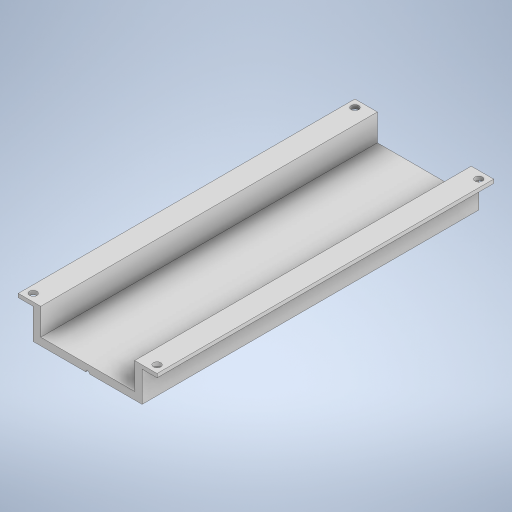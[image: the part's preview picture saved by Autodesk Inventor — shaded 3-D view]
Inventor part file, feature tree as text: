
AUTODESK INVENTOR PART (.ipt)
format: ipt  version: 2023 (Build 270158000, 158)  size: 281,600 bytes
history: native  units: mm
features: extrude x2, sketch x2
ambient origin geometry x8: Origin, YZ Plane, XZ Plane, XY Plane, X Axis, Y Axis, Z Axis, Center Point
bodies: Solid1 (feature_tree)
feature tree (4):
  extrude  "Extrusion1"  Depth=35.75mm
  extrude  "Extrusion2"  Depth=450.0mm TaperAngle=0.0deg
  sketch  "Sketch1"  dims[d0=10.0mm d1=35.75mm]
  sketch  "Sketch2"  dims[d2=10.0mm d3=450.0mm d4=0.0mm d5=20.0mm d6=10.0mm d7=20.0mm d8=20.0mm d9=20.0mm d10=20.0mm d11=20.0mm d12=20.0mm d13=10.0mm d14=10.0mm d15=10.0mm d16=450.0mm d17=0.0mm]
